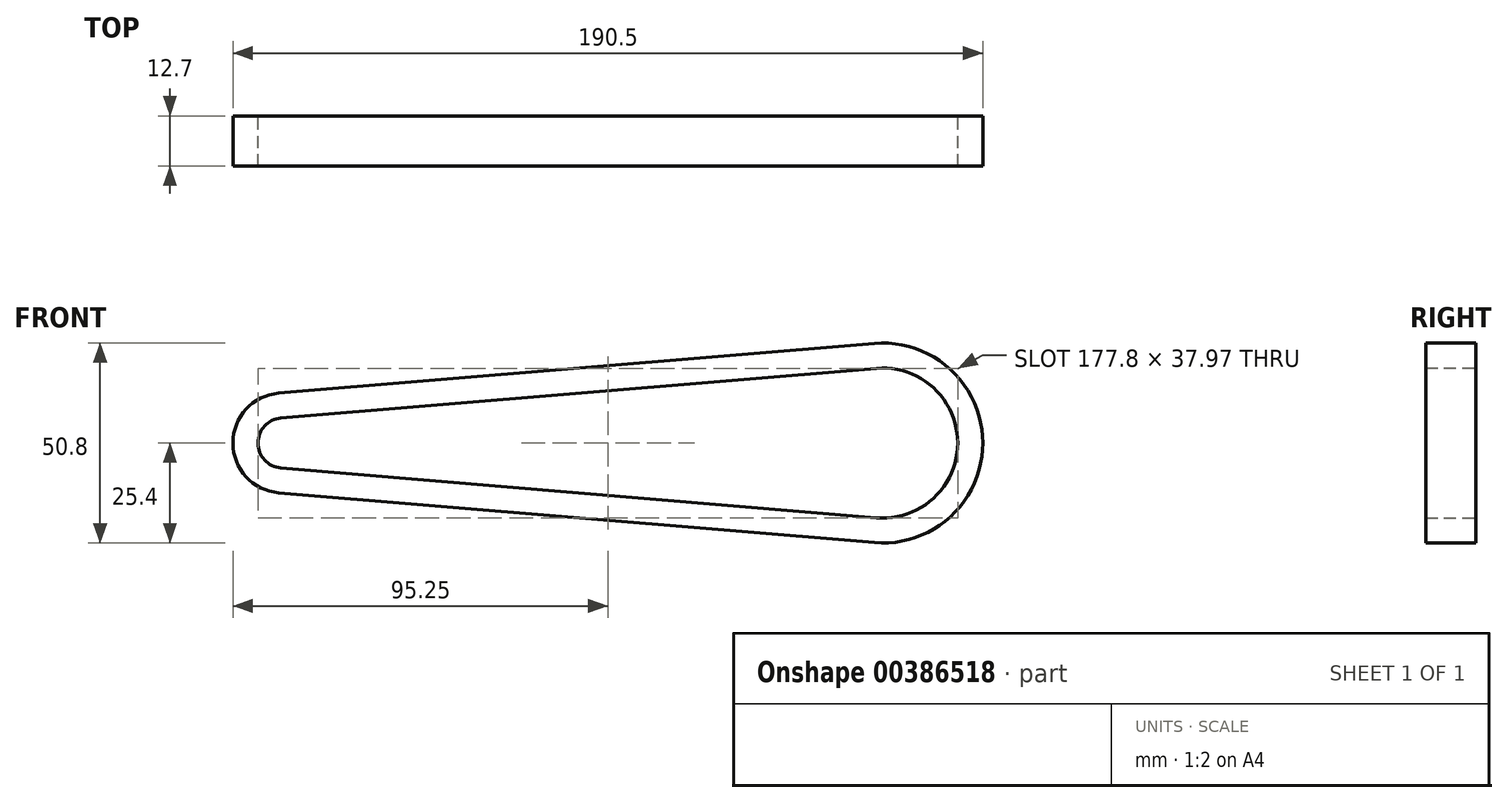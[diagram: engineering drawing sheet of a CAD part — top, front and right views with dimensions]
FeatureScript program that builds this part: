
annotation { "Feature Type Name" : "Feature", "Feature Type Description" : "" }
export const myFeature = defineFeature(function(context is Context, id is Id, definition is map)
    precondition{}
    {
        {
            var Q0;
            Q0=qCreatedBy(makeId("Front.planeOp"),FACE);
            var sketch = newSketch(context, id + "F0", { "sketchPlane" : qUnion([Q0])});
            skArc(sketch, "E0", {"start": v(-2.12, -25.31) * mm, "mid": v(25.4, 0) * mm, "end": v(-2.12, 25.31) * mm});
            skArc(sketch, "E1", {"start": v(-153.46, 12.66) * mm, "mid": v(-165.1, 0) * mm, "end": v(-153.46, -12.66) * mm});
            skLineSegment(sketch, "E2", {"start": v(-153.46, 12.66) * mm, "end": v(-2.12, 25.31) * mm});
            skLineSegment(sketch, "E3", {"start": v(-153.46, -12.66) * mm, "end": v(-2.12, -25.31) * mm});
            skLineSegment(sketch, "E4.0", {"start": v(-152.93, 6.33) * mm, "end": v(-1.59, 18.98) * mm});
            skArc(sketch, "E4.1", {"start": v(-152.93, 6.33) * mm, "mid": v(-158.75, 0) * mm, "end": v(-152.93, -6.33) * mm});
            skLineSegment(sketch, "E4.2", {"start": v(-152.93, -6.33) * mm, "end": v(-1.59, -18.98) * mm});
            skArc(sketch, "E4.3", {"start": v(-1.59, -18.98) * mm, "mid": v(19.05, 0) * mm, "end": v(-1.59, 18.98) * mm});
            skSolve(sketch);
        }
        {
            var Q0;
            Q0=makeQuery(id+"F0.imprint","IMPRINT",FACE,{"disambiguationData":[TD([[makeQuery(id+"F0.imprint","IMPRINT",EDGE,{"derivedFrom":sQuery(id+"F0.wireOp",EDGE,"E0")}),1.0]])]});
            extrude(context, id + "F1", {"entities" : qUnion([Q0]), "depth" : 12.7 * mm});
        }
    });
